# Revit family: P191568KX-007c_KBSD602E
name_source: partatom
category: Specialty Equipment
units: mm (PartAtom-declared; Revit-internal decimal feet)

## family parameters
Always vertical = Yes
Cut with Voids When Loaded = No
Enable Cutting in Views = No
Maintain Annotation Orientation = No
Part Type = Normal
Room Calculation Point = No
Round Connector Dimension = Use Diameter
Shared = No
Work Plane-Based = No

## types (1)
- KBSD602ESS
    Accent Material = ARCAT - Glass - Gray
    Amps = 15 A
    Body Material = ARCAT - Metal - Steel - Stainless
    Clearance Material = ARCAT - Clearance
    Default Elevation = 0"
    Depth = 27 3/4"
    Description = 25.0 cu. ft 42-Inch Width Built-In Side by Side Refrigerator with PrintShield™ Finish
Réfrigérateur encastré côte à côte de 25,5 pi³ et 42 po de largeur
    Dimension Guide = http://access.whirlpool.com Guide&sku=KBSD602ESS&language=EN
http://access.whirlpool.com Guide&sku=KBSD602ESS&language=EN
    Display Material = ARCAT - Glass - Black
    Door Material = ARCAT - Metal - Steel - Stainless
    Energy Guide = http://access.whirlpool.com Guide&sku=KBSD602ESS&language=EN
http://access.whirlpool.com Guide&sku=KBSD602ESS&language=FR
    Family Name = REFRIGERATION
    Feature 1 = PrintShield™ Finish
Fini PrintShield™
    Feature 2 = ExtendFresh™ Plus Temperature Management System
Système de gestion de la température ExtendFresh™
    Feature 3 = Produce Preserver
Conservateur de fruits et légumes
    Handle Material = ARCAT - Metal - Steel - Gray
    Height = 83 3/8"
    Installation-Fabrication = http://access.whirlpool.com Instruction&sku=KBSD602ESS&language=EN
http://access.whirlpool.com Instruction&sku=KBSD602ESS&language=FR
    Manufacturer = KitchenAid
    Model = KBSD602ESS
    Panel Material = ARCAT - Metal - Steel - Black
    Switch Material = ARCAT - Plastic - Gray
    Voltage = 0 V
    Wheel Material = ARCAT - Plastic - Black
    Width = 42 1/4"

## geometry (parser evidence)
native form markers: Sweep x5
no freeform markers — native parametric forms only
